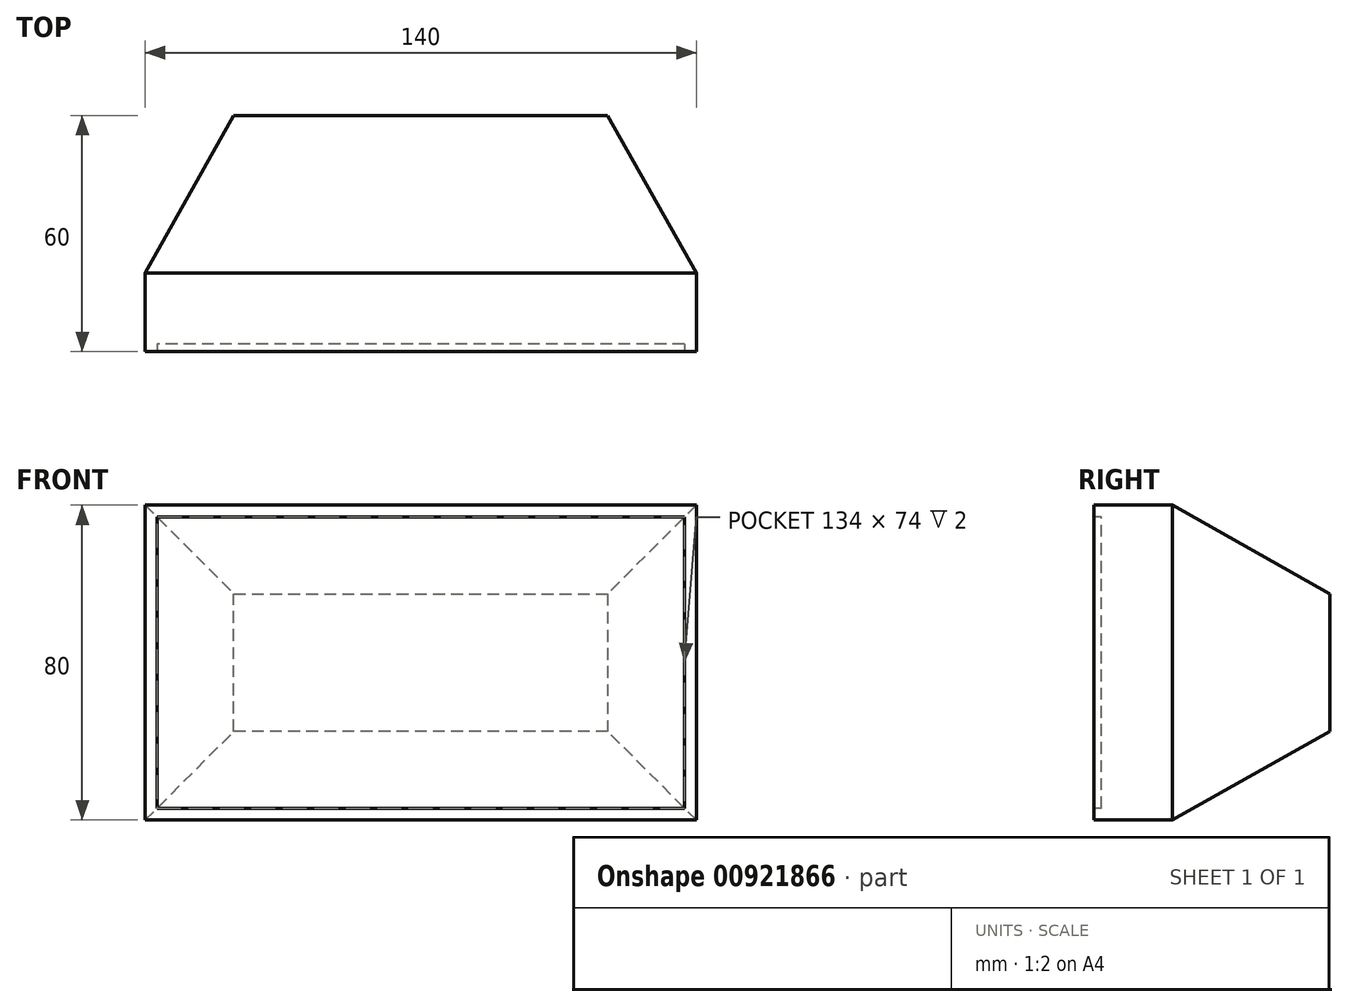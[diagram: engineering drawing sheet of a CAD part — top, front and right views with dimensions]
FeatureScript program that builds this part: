
annotation { "Feature Type Name" : "Feature", "Feature Type Description" : "" }
export const myFeature = defineFeature(function(context is Context, id is Id, definition is map)
    precondition{}
    {
        {
            var Q0;
            Q0=qCreatedBy(makeId("Front.planeOp"),FACE);
            var sketch = newSketch(context, id + "F0", { "sketchPlane" : qUnion([Q0])});
            skLineSegment(sketch, "E0.bottom", {"start": v(70, -40) * mm, "end": v(-70, -40) * mm});
            skLineSegment(sketch, "E0.top", {"start": v(70, 40) * mm, "end": v(-70, 40) * mm});
            skLineSegment(sketch, "E0.left", {"start": v(70, -40) * mm, "end": v(70, 40) * mm});
            skLineSegment(sketch, "E0.right", {"start": v(-70, -40) * mm, "end": v(-70, 40) * mm});
            skPoint(sketch, "E0.middle", {"position": v(0, 0) * mm});
            skSolve(sketch);
        }
        {
            var Q0;
            Q0=makeQuery(id+"F0.imprint","IMPRINT",FACE,{"disambiguationData":[TD([[makeQuery(id+"F0.imprint","IMPRINT",EDGE,{"derivedFrom":sQuery(id+"F0.wireOp",EDGE,"E0.bottom")}),-1.0]])]});
            extrude(context, id + "F1", {"entities" : qUnion([Q0]), "depth" : 60 * mm, "offsetDistance" : 25 * mm});
        }
        {
            var Q0;
            Q0=makeQuery(id+"F1.opExtrude","CAP_FACE",FACE,{"disambiguationData":[OSD([sQuery(id+"F0.wireOp",EDGE,"E0.bottom"),sQuery(id+"F0.wireOp",EDGE,"E0.top"),sQuery(id+"F0.wireOp",EDGE,"E0.left"),sQuery(id+"F0.wireOp",EDGE,"E0.right")])],"isStart":true});
            chamfer(context, id + "F2", {"entities" : qUnion([Q0]), "chamferType" : ChamferType.TWO_OFFSETS, "width1" : 22.5 * mm, "oppositeDirection" : false, "width2" : 40 * mm, "tangentPropagation" : true});
        }
        {
            var Q0;
            Q0=makeQuery(id+"F1.opExtrude","CAP_FACE",FACE,{"disambiguationData":[OSD([sQuery(id+"F0.wireOp",EDGE,"E0.bottom"),sQuery(id+"F0.wireOp",EDGE,"E0.top"),sQuery(id+"F0.wireOp",EDGE,"E0.left"),sQuery(id+"F0.wireOp",EDGE,"E0.right")])],"isStart":false});
            var sketch = newSketch(context, id + "F3", { "sketchPlane" : qUnion([Q0])});
            skLineSegment(sketch, "E1.bottom", {"start": v(67, -37) * mm, "end": v(-67, -37) * mm});
            skLineSegment(sketch, "E1.top", {"start": v(67, 37) * mm, "end": v(-67, 37) * mm});
            skLineSegment(sketch, "E1.left", {"start": v(67, -37) * mm, "end": v(67, 37) * mm});
            skLineSegment(sketch, "E1.right", {"start": v(-67, -37) * mm, "end": v(-67, 37) * mm});
            skPoint(sketch, "E1.middle", {"position": v(0, 0) * mm});
            skSolve(sketch);
        }
        {
            var Q0;
            Q0=makeQuery(id+"F3.imprint","IMPRINT",FACE,{"disambiguationData":[TD([[makeQuery(id+"F3.imprint","IMPRINT",EDGE,{"derivedFrom":sQuery(id+"F3.wireOp",EDGE,"E1.bottom")}),-1.0]])]});
            extrude(context, id + "F4", {"entities" : qUnion([Q0]), "operationType" : NewBodyOperationType.ADD, "oppositeDirection" : true, "depth" : 2 * mm, "offsetDistance" : 25 * mm});
        }
        {
            var Q0;
            Q0=makeQuery(id+"F3.imprint","IMPRINT",FACE,{"disambiguationData":[TD([[makeQuery(id+"F3.imprint","IMPRINT",EDGE,{"derivedFrom":sQuery(id+"F3.wireOp",EDGE,"E1.bottom")}),-1.0]])]});
            extrude(context, id + "F5", {"entities" : qUnion([Q0]), "operationType" : NewBodyOperationType.REMOVE, "oppositeDirection" : true, "depth" : 2 * mm, "offsetDistance" : 25 * mm});
        }
    });
